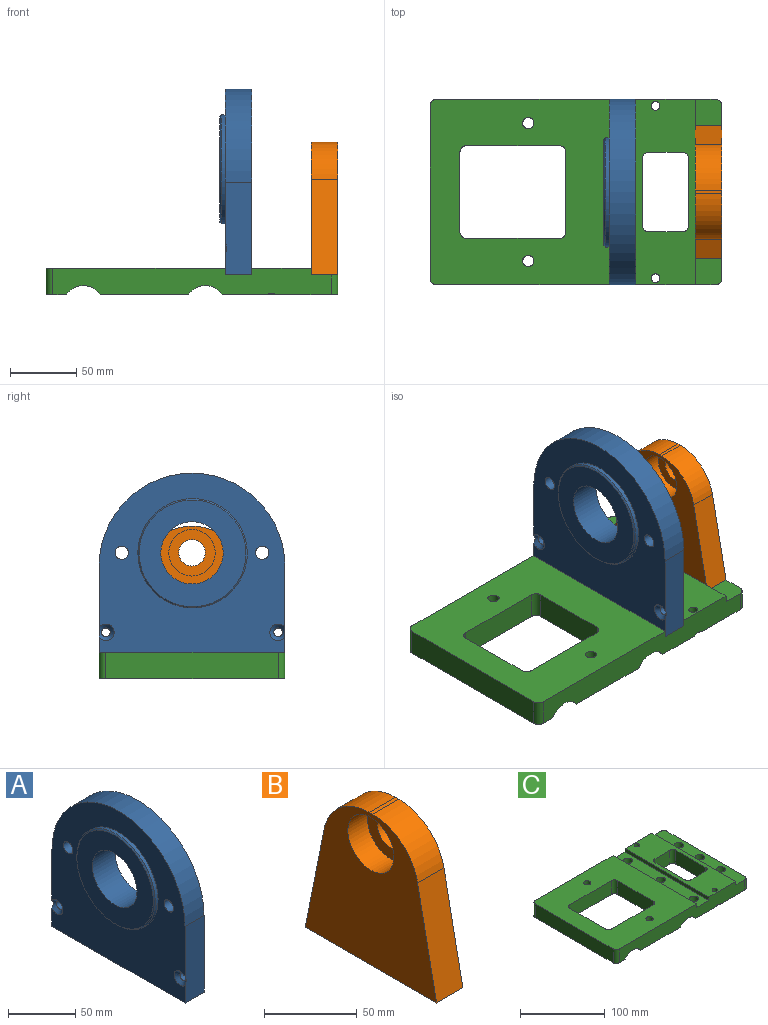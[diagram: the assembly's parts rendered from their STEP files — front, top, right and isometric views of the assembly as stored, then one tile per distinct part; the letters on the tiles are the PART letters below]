
ASSEMBLY  parts=3 mates=2
PART A: 22 faces, bbox 24x142.6x140 mm
  f0: plane 70x20mm, normal (0,-1,0), area 1393.5mm2, adj f1,f6,f7,f17,f21
  f1: plane 140x20mm, normal (0,0,-1), area 2629.8mm2, adj f0,f2,f6,f7,f12,f14,f16
  f2: plane 70x20mm, normal (0,1,0), area 1393.5mm2, adj f1,f6,f7,f17,f20
  f3: cylinder r=5mm len=20mm, axis (-1,0,0), area 628.3mm2, adj f6,f7
  f4: cylinder r=5mm len=20mm, axis (-1,0,0), area 628.3mm2, adj f6,f7
  f5: cylinder r=23.5mm len=47mm, axis (-1,0,0), area 3543.7mm2, adj f6,f9
  f6: plane 140x140mm, normal (1,0,0), area 15536.5mm2, adj f0,f1,f2,f3,f4,f5,f17,f18
  f7: plane 140x140mm, normal (-1,0,0), area 11758.4mm2, adj f0,f1,f2,f3,f4,f8,f17,f20
  f8: cylinder r=41.25mm len=82.5mm, axis (1,0,0), area 777.5mm2, adj f7,f10
  f9: plane 80.5x80.5mm, normal (-1,0,0), area 3354.6mm2, adj f5,f10
  f10: cone r=41.25mm half-angle=45deg, axis (1,0,0), area 362.1mm2, adj f8,f9
  f11: cone r=0mm half-angle=59deg, axis (0,0,-1), area 66.2mm2, adj f12
  f12: cylinder r=4.25mm len=60mm, axis (0,0,-1), area 1602.2mm2, adj f1,f11
  f13: cone r=0mm half-angle=59deg, axis (0,0,-1), area 66.2mm2, adj f14
  f14: cylinder r=4.25mm len=60mm, axis (0,0,-1), area 1602.2mm2, adj f1,f13
  f15: cone r=0mm half-angle=59deg, axis (0,0,-1), area 66.2mm2, adj f16
  f16: cylinder r=4.25mm len=50mm, axis (0,0,-1), area 1335.2mm2, adj f1,f15
  f17: cylinder r=70mm len=140mm, axis (-1,0,0), area 4398.2mm2, adj f0,f2,f6,f7
  f18: cylinder r=3.3mm len=17mm, axis (-1,0,0), area 352.5mm2, adj f6,f21
  f19: cylinder r=3.3mm len=17mm, axis (-1,0,0), area 352.5mm2, adj f6,f20
  f20: cone r=3.3mm half-angle=45deg, axis (-1,0,0), area 118.3mm2, adj f2,f7,f19
  f21: cone r=3.3mm half-angle=45deg, axis (-1,0,0), area 118.3mm2, adj f0,f7,f18
PART B: 17 faces, bbox 20x100x100 mm
  f0: plane 71.86x20mm, normal (0,-0.98,0.2), area 1465.7mm2, adj f1,f5,f6,f16
  f1: plane 100x20mm, normal (0,0,-1), area 1829.8mm2, adj f0,f2,f5,f6,f10,f12,f14
  f2: plane 71.86x20mm, normal (0,0.98,0.2), area 1465.7mm2, adj f1,f5,f6,f15
  f3: plane 20x2.61mm, normal (0,0,1), area 52.3mm2, adj f5,f6,f15,f16
  f4: cylinder r=10mm len=20mm, axis (-1,0,0), area 314.2mm2, adj f5,f8
  f5: plane 100x100mm, normal (1,0,0), area 7359.7mm2, adj f0,f1,f2,f3,f4,f15,f16
  f6: plane 100x100mm, normal (-1,0,0), area 6711.8mm2, adj f0,f1,f2,f3,f7,f15,f16
  f7: cylinder r=17.5mm len=35mm, axis (-1,0,0), area 1649.3mm2, adj f6,f8
  f8: plane 35x35mm, normal (-1,0,0), area 648mm2, adj f4,f7
  f9: cone r=0mm half-angle=59deg, axis (0,0,-1), area 66.2mm2, adj f10
  f10: cylinder r=4.25mm len=42.1mm, axis (0,0,-1), area 1124.2mm2, adj f1,f9
  f11: cone r=0mm half-angle=59deg, axis (0,0,-1), area 66.2mm2, adj f12
  f12: cylinder r=4.25mm len=42.1mm, axis (0,0,-1), area 1124.2mm2, adj f1,f11
  f13: cone r=0mm half-angle=59deg, axis (0,0,-1), area 66.2mm2, adj f14
  f14: cylinder r=4.25mm len=42.1mm, axis (0,0,-1), area 1124.2mm2, adj f1,f13
  f15: cylinder r=35mm len=34.32mm, axis (-1,0,0), area 961.4mm2, adj f2,f3,f5,f6
  f16: cylinder r=35mm len=34.32mm, axis (-1,0,0), area 961.4mm2, adj f0,f3,f5,f6
PART C: 54 faces, bbox 220.5x142.6x20 mm
  f0: plane 140x66.62mm, normal (0,0,-1), area 4901mm2, adj f2,f7,f9,f23,f30,f31,f36,f38
  f1: plane 140x135mm, normal (0,0,1), area 13197.2mm2, adj f7,f8,f9,f11,f30,f31,f32,f33
  f2: cylinder r=15mm len=140mm, axis (0,1,0), area 2789.5mm2, adj f0,f3,f7,f9,f36,f37,f38,f40
  f3: plane 140x15.31mm, normal (0,0,-1), area 2132.9mm2, adj f2,f7,f8,f9,f32,f33
  f4: plane 140x45mm, normal (0,0,1), area 4153mm2, adj f7,f9,f10,f13,f15,f16,f17,f18
  f5: plane 140x87.31mm, normal (0,0,-1), area 7826.8mm2, adj f6,f7,f9,f15,f16,f17,f18,f19
  f6: plane 130x15mm, normal (1,0,0), area 1943.6mm2, adj f5,f14,f34,f35,f46,f47,f48
  f7: plane 210x20mm, normal (0,1,0), area 3767.8mm2, adj f0,f1,f2,f3,f4,f5,f10,f11
  f8: plane 130x20mm, normal (-1,0,0), area 2600mm2, adj f1,f3,f32,f33
  f9: plane 210x20mm, normal (0,-1,0), area 3767.8mm2, adj f0,f1,f2,f3,f4,f5,f10,f11
  f10: plane 140x5mm, normal (-1,0,0), area 700mm2, adj f4,f7,f9,f12
  f11: plane 140x5mm, normal (1,0,0), area 700mm2, adj f1,f7,f9,f12
  f12: plane 140x20mm, normal (0,0,1), area 2514.9mm2, adj f7,f9,f10,f11,f24,f25,f26
  f13: plane 140x5mm, normal (1,0,0), area 700mm2, adj f4,f7,f9,f14
  f14: plane 140x20mm, normal (0,0,1), area 2504.2mm2, adj f6,f7,f9,f13,f27,f28,f29,f34
  f15: plane 25x20mm, normal (0,-1,0), area 500mm2, adj f4,f5,f19,f22
  f16: plane 50x20mm, normal (1,0,0), area 1000mm2, adj f4,f5,f19,f20
  f17: plane 25x20mm, normal (0,1,0), area 500mm2, adj f4,f5,f20,f21
  f18: plane 50x20mm, normal (-1,0,0), area 1000mm2, adj f4,f5,f21,f22
  f19: cylinder r=5mm len=20mm, axis (0,0,1), area 157.1mm2, adj f4,f5,f15,f16
  f20: cylinder r=5mm len=20mm, axis (0,0,-1), area 157.1mm2, adj f4,f5,f16,f17
  f21: cylinder r=5mm len=20mm, axis (0,0,1), area 157.1mm2, adj f4,f5,f17,f18
  f22: cylinder r=5mm len=20mm, axis (0,0,-1), area 157.1mm2, adj f4,f5,f15,f18
  f23: cylinder r=15mm len=140mm, axis (0,1,0), area 4234.7mm2, adj f0,f5,f7,f9
  f24: cylinder r=5.5mm len=11mm, axis (0,0,1), area 345.6mm2, adj f12,f49
  f25: cylinder r=5.5mm len=11mm, axis (0,0,1), area 345.6mm2, adj f12,f50
  f26: cylinder r=5.5mm len=11mm, axis (0,0,1), area 345.6mm2, adj f12,f51
  f27: cylinder r=5.5mm len=11mm, axis (0,0,1), area 345.6mm2, adj f14,f48
  f28: cylinder r=5.5mm len=11mm, axis (0,0,1), area 345.6mm2, adj f14,f47
  f29: cylinder r=5.5mm len=11mm, axis (0,0,1), area 345.6mm2, adj f14,f46
  f30: cylinder r=4.25mm len=20mm, axis (0,0,-1), area 534.1mm2, adj f0,f1
  f31: cylinder r=4.25mm len=20mm, axis (0,0,-1), area 534.1mm2, adj f0,f1
  f32: cylinder r=5mm len=20mm, axis (0,0,1), area 157.1mm2, adj f1,f3,f7,f8
  f33: cylinder r=5mm len=20mm, axis (0,0,-1), area 157.1mm2, adj f1,f3,f8,f9
  f34: cylinder r=5mm len=15mm, axis (0,0,1), area 117.8mm2, adj f5,f6,f9,f14
  f35: cylinder r=5mm len=15mm, axis (0,0,-1), area 117.8mm2, adj f5,f6,f7,f14
  f36: plane 70x20mm, normal (0,-1,0), area 1333.5mm2, adj f0,f1,f2,f40,f43
  f37: plane 60x14.06mm, normal (1,0,0), area 843.8mm2, adj f1,f2,f40,f41
  f38: plane 70x20mm, normal (0,1,0), area 1333.5mm2, adj f0,f1,f2,f41,f42
  f39: plane 60x20mm, normal (-1,0,0), area 1200mm2, adj f0,f1,f42,f43
  f40: cylinder r=5mm len=14.06mm, axis (0,0,1), area 106.5mm2, adj f1,f2,f36,f37
  f41: cylinder r=5mm len=14.06mm, axis (0,0,-1), area 106.5mm2, adj f1,f2,f37,f38
  f42: cylinder r=5mm len=20mm, axis (0,0,1), area 157.1mm2, adj f0,f1,f38,f39
  f43: cylinder r=5mm len=20mm, axis (0,0,-1), area 157.1mm2, adj f0,f1,f36,f39
  f44: cylinder r=3.3mm len=17mm, axis (0,0,1), area 352.5mm2, adj f4,f52
  f45: cylinder r=3.3mm len=17mm, axis (0,0,1), area 352.5mm2, adj f4,f53
  f46: cone r=5.5mm half-angle=45deg, axis (0,0,-1), area 352.4mm2, adj f5,f6,f29
  f47: cone r=5.5mm half-angle=45deg, axis (0,0,-1), area 352.4mm2, adj f5,f6,f28
  f48: cone r=5.5mm half-angle=45deg, axis (0,0,-1), area 352.4mm2, adj f5,f6,f27
  f49: cone r=5.5mm half-angle=45deg, axis (0,0,-1), area 355.4mm2, adj f5,f24
  f50: cone r=5.5mm half-angle=45deg, axis (0,0,-1), area 355.4mm2, adj f5,f25
  f51: cone r=5.5mm half-angle=45deg, axis (0,0,-1), area 355.4mm2, adj f5,f26
  f52: cone r=3.3mm half-angle=45deg, axis (0,0,-1), area 118.3mm2, adj f5,f7,f44
  f53: cone r=3.3mm half-angle=45deg, axis (0,0,-1), area 118.3mm2, adj f5,f9,f45
PLACE A t=(135,0,15)mm
PLACE B t=(199.96,20,15)mm
PLACE C at identity fixed
MATE slider A.f15 <-> C.f25  axis (0,0,-1) through (145,70,15)mm
MATE fastened B.f11 <-> C.f14  axis (0,0,-1) through (209.96,70,15)mm
